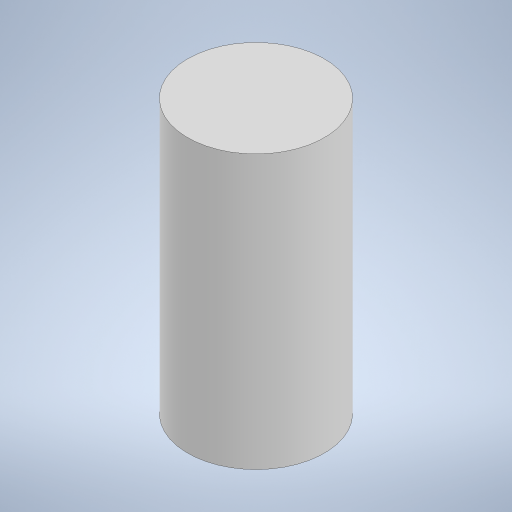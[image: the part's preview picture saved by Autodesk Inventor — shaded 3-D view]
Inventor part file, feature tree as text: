
AUTODESK INVENTOR PART (.ipt)
format: ipt  version: 2023.1 (Build 271208000, 208)  size: 199,168 bytes
history: native  units: mm
features: extrude x1, sketch x1
ambient origin geometry x8: Origin, YZ Plane, XZ Plane, XY Plane, X Axis, Y Axis, Z Axis, Center Point
bodies: Solid1 (feature_tree)
feature tree (2):
  extrude  "Extrusion1"  Depth=8.0mm TaperAngle=0.0deg
  sketch  "Sketch1"  dims[d0=4.0mm d1=8.0mm d2=0.0mm]
